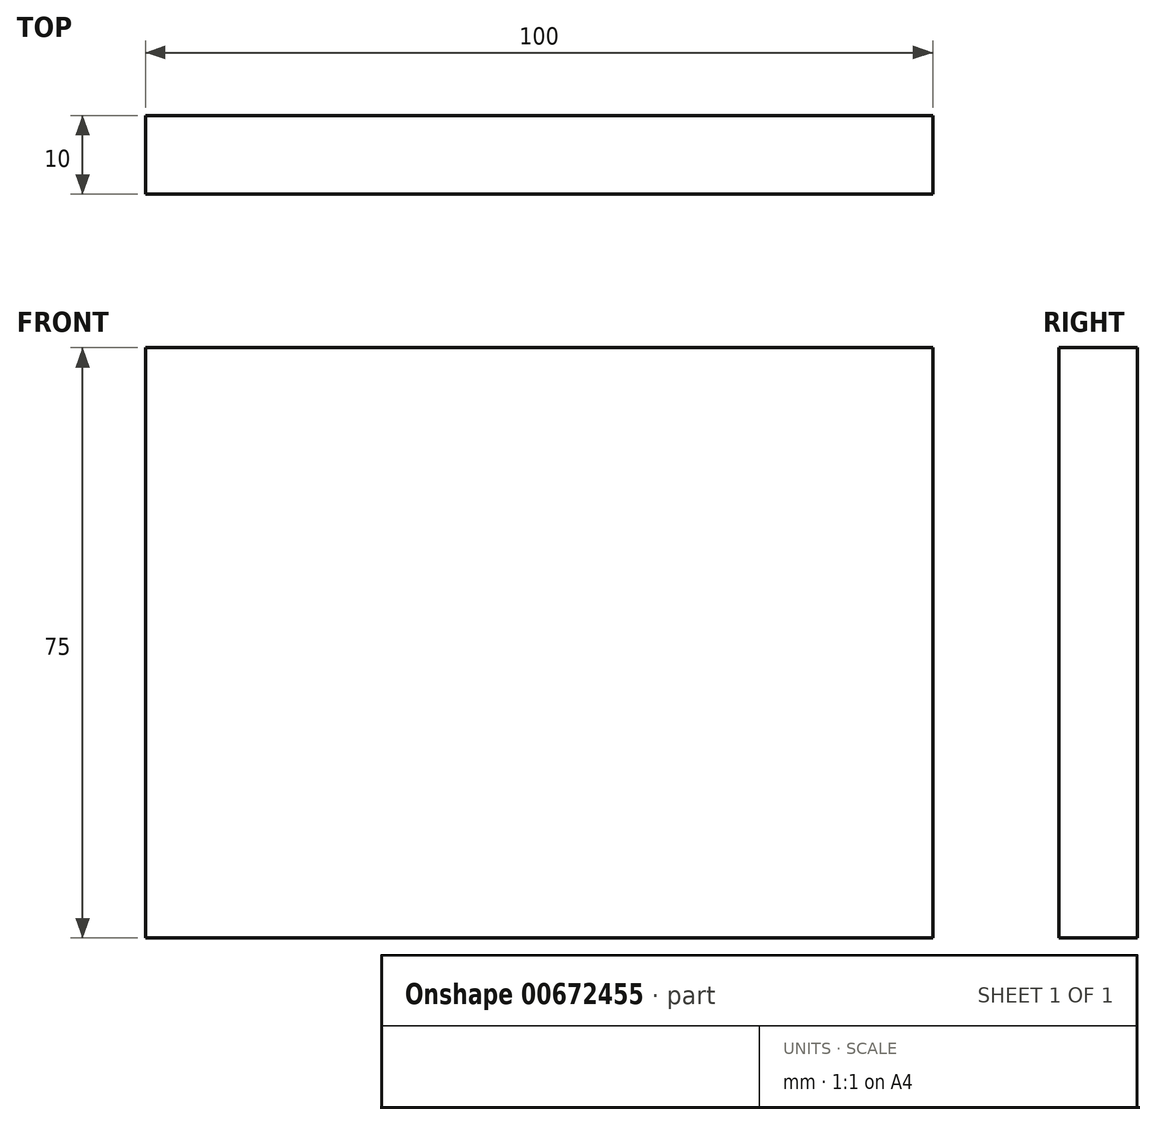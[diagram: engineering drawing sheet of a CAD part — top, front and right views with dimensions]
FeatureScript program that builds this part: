
annotation { "Feature Type Name" : "Feature", "Feature Type Description" : "" }
export const myFeature = defineFeature(function(context is Context, id is Id, definition is map)
    precondition{}
    {
        {
            var Q0;
            Q0=qCreatedBy(makeId("Front.planeOp"),FACE);
            var sketch = newSketch(context, id + "F0", { "sketchPlane" : qUnion([Q0])});
            skLineSegment(sketch, "E0.bottom", {"start": v(50, -37.5) * mm, "end": v(-50, -37.5) * mm});
            skLineSegment(sketch, "E0.top", {"start": v(50, 37.5) * mm, "end": v(-50, 37.5) * mm});
            skLineSegment(sketch, "E0.left", {"start": v(50, -37.5) * mm, "end": v(50, 37.5) * mm});
            skLineSegment(sketch, "E0.right", {"start": v(-50, -37.5) * mm, "end": v(-50, 37.5) * mm});
            skPoint(sketch, "E0.middle", {"position": v(0, 0) * mm});
            skSolve(sketch);
        }
        {
            var Q0;
            Q0 = qSketchRegion(id + "F0", true);
            extrude(context, id + "F1", {"entities" : qUnion([Q0]), "depth" : 10 * mm, "offsetDistance" : 25 * mm});
        }
    });
